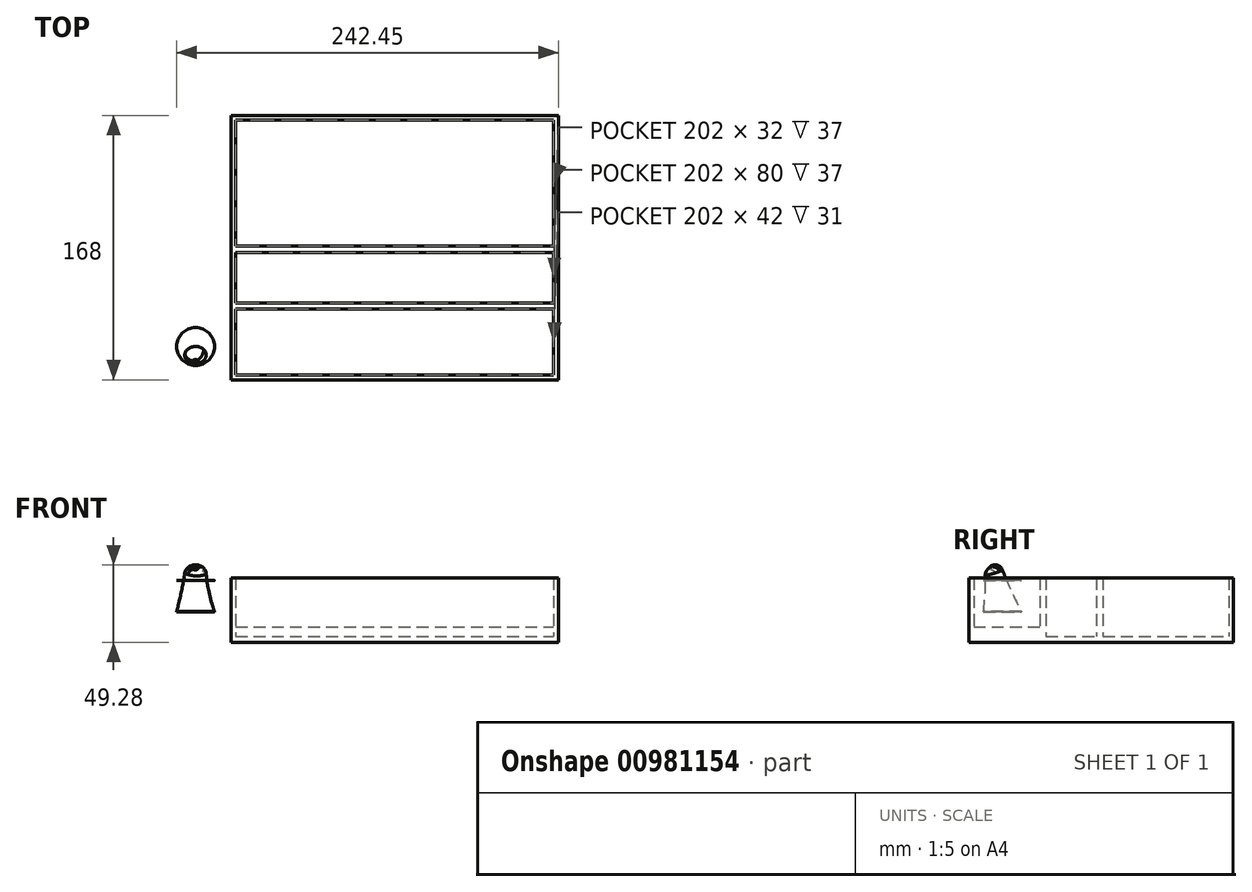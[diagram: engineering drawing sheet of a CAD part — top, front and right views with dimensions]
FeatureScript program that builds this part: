
annotation { "Feature Type Name" : "Feature", "Feature Type Description" : "" }
export const myFeature = defineFeature(function(context is Context, id is Id, definition is map)
    precondition{}
    {
        {
            var Q0;
            Q0=qCreatedBy(makeId("Top.planeOp"),FACE);
            var sketch = newSketch(context, id + "F0", { "sketchPlane" : qUnion([Q0])});
            skLineSegment(sketch, "E0.bottom", {"start": v(104, -84) * mm, "end": v(-104, -84) * mm});
            skLineSegment(sketch, "E0.top", {"start": v(104, 84) * mm, "end": v(-104, 84) * mm});
            skLineSegment(sketch, "E0.left", {"start": v(104, -84) * mm, "end": v(104, 84) * mm});
            skLineSegment(sketch, "E0.right", {"start": v(-104, -84) * mm, "end": v(-104, 84) * mm});
            skPoint(sketch, "E0.middle", {"position": v(0, 0) * mm});
            skSolve(sketch);
        }
        {
            var Q0;
            Q0=makeQuery(id+"F0.imprint","IMPRINT",FACE,{"disambiguationData":[TD([[makeQuery(id+"F0.imprint","IMPRINT",EDGE,{"derivedFrom":sQuery(id+"F0.wireOp",EDGE,"E0.bottom")}),-1.0]])]});
            extrude(context, id + "F1", {"entities" : qUnion([Q0]), "depth" : 4 * mm, "offsetDistance" : 25 * mm});
        }
        {
            var Q0;
            Q0=makeQuery(id+"F1.opExtrude","CAP_FACE",FACE,{"disambiguationData":[OSD([sQuery(id+"F0.wireOp",EDGE,"E0.bottom"),sQuery(id+"F0.wireOp",EDGE,"E0.top"),sQuery(id+"F0.wireOp",EDGE,"E0.left"),sQuery(id+"F0.wireOp",EDGE,"E0.right")])],"isStart":false});
            var sketch = newSketch(context, id + "F2", { "sketchPlane" : qUnion([Q0])});
            skLineSegment(sketch, "E1.bottom", {"start": v(104, -84) * mm, "end": v(-104, -84) * mm});
            skLineSegment(sketch, "E1.top", {"start": v(104, 84) * mm, "end": v(-104, 84) * mm});
            skLineSegment(sketch, "E1.left", {"start": v(104, -84) * mm, "end": v(104, 84) * mm});
            skLineSegment(sketch, "E1.right", {"start": v(-104, -84) * mm, "end": v(-104, 84) * mm});
            skPoint(sketch, "E1.middle", {"position": v(0, 0) * mm});
            skLineSegment(sketch, "E2.bottom", {"start": v(101, -81) * mm, "end": v(-101, -81) * mm});
            skLineSegment(sketch, "E2.top", {"start": v(101, 81) * mm, "end": v(-101, 81) * mm});
            skLineSegment(sketch, "E2.left", {"start": v(101, -81) * mm, "end": v(101, 81) * mm});
            skLineSegment(sketch, "E2.right", {"start": v(-101, -81) * mm, "end": v(-101, 81) * mm});
            skLineSegment(sketch, "E3", {"start": v(-101, 81) * mm, "end": v(-101, 41) * mm, "construction": true});
            skLineSegment(sketch, "E4", {"start": v(-101, 41) * mm, "end": v(-101, 1) * mm, "construction": true});
            skLineSegment(sketch, "E5", {"start": v(-101, 1) * mm, "end": v(-101, -35) * mm, "construction": true});
            skLineSegment(sketch, "E6.bottom", {"start": v(-101, 41) * mm, "end": v(101, 41) * mm});
            skLineSegment(sketch, "E6.top", {"start": v(-101, 37) * mm, "end": v(101, 37) * mm});
            skLineSegment(sketch, "E6.left", {"start": v(-101, 41) * mm, "end": v(-101, 37) * mm});
            skLineSegment(sketch, "E6.right", {"start": v(101, 41) * mm, "end": v(101, 37) * mm});
            skLineSegment(sketch, "E7.bottom", {"start": v(-101, 1) * mm, "end": v(101, 1) * mm});
            skLineSegment(sketch, "E7.top", {"start": v(-101, -3) * mm, "end": v(101, -3) * mm});
            skLineSegment(sketch, "E7.left", {"start": v(-101, 1) * mm, "end": v(-101, -3) * mm});
            skLineSegment(sketch, "E7.right", {"start": v(101, 1) * mm, "end": v(101, -3) * mm});
            skLineSegment(sketch, "E8.bottom", {"start": v(-101, -35) * mm, "end": v(101, -35) * mm});
            skLineSegment(sketch, "E8.top", {"start": v(-101, -39) * mm, "end": v(101, -39) * mm});
            skLineSegment(sketch, "E8.left", {"start": v(-101, -35) * mm, "end": v(-101, -39) * mm});
            skLineSegment(sketch, "E8.right", {"start": v(101, -35) * mm, "end": v(101, -39) * mm});
            skLineSegment(sketch, "E9", {"start": v(-101, 81) * mm, "end": v(-42, 81) * mm, "construction": true});
            skLineSegment(sketch, "E10", {"start": v(-42, 81) * mm, "end": v(-2, 81) * mm, "construction": true});
            skLineSegment(sketch, "E11", {"start": v(-2, 81) * mm, "end": v(38, 81) * mm, "construction": true});
            skLineSegment(sketch, "E12", {"start": v(38, 81) * mm, "end": v(101, 81) * mm, "construction": true});
            skLineSegment(sketch, "E13.bottom", {"start": v(-42, 81) * mm, "end": v(-38, 81) * mm});
            skLineSegment(sketch, "E13.top", {"start": v(-42, 41) * mm, "end": v(-38, 41) * mm});
            skLineSegment(sketch, "E13.left", {"start": v(-42, 81) * mm, "end": v(-42, 41) * mm});
            skLineSegment(sketch, "E13.right", {"start": v(-38, 81) * mm, "end": v(-38, 41) * mm});
            skLineSegment(sketch, "E14.bottom", {"start": v(-2, 81) * mm, "end": v(2, 81) * mm});
            skLineSegment(sketch, "E14.top", {"start": v(-2, 41) * mm, "end": v(2, 41) * mm});
            skLineSegment(sketch, "E15.bottom", {"start": v(38, 81) * mm, "end": v(42, 81) * mm});
            skLineSegment(sketch, "E15.top", {"start": v(38, 41) * mm, "end": v(42, 41) * mm});
            skLineSegment(sketch, "E15.left", {"start": v(38, 81) * mm, "end": v(38, 41) * mm});
            skLineSegment(sketch, "E15.right", {"start": v(42, 81) * mm, "end": v(42, 41) * mm});
            skLineSegment(sketch, "E16.bottom", {"start": v(-2, 37) * mm, "end": v(2, 37) * mm});
            skLineSegment(sketch, "E16.top", {"start": v(-2, 1) * mm, "end": v(2, 1) * mm});
            skLineSegment(sketch, "E16.left", {"start": v(-2, 37) * mm, "end": v(-2, 1) * mm});
            skLineSegment(sketch, "E16.right", {"start": v(2, 37) * mm, "end": v(2, 1) * mm});
            skSolve(sketch);
        }
        {
            var Q0;
            Q0=makeQuery(id+"F2.imprint","IMPRINT",FACE,{"disambiguationData":[TD([[makeQuery(id+"F2.imprint","IMPRINT",EDGE,{"derivedFrom":sQuery(id+"F2.wireOp",EDGE,"E1.bottom")}),-1.0]])]});
            var Q1;
            {var subQ2=sQuery(id+"F2.wireOp",EDGE,"E6.left");Q1=makeQuery(id+"F2.imprint","IMPRINT",FACE,{"disambiguationData":[TD([[makeQuery(id+"F2.imprint","IMPRINT",EDGE,{"derivedFrom":subQ2}),1.0]])]});}
            var Q2;
            Q2=makeQuery(id+"F2.imprint","IMPRINT",FACE,{"disambiguationData":[TD([[makeQuery(id+"F2.imprint","IMPRINT",EDGE,{"derivedFrom":sQuery(id+"F2.wireOp",EDGE,"E13.bottom")}),-1.0]])]});
            var Q3;
            Q3=makeQuery(id+"F2.imprint","IMPRINT",FACE,{"disambiguationData":[TD([[makeQuery(id+"F2.imprint","IMPRINT",EDGE,{"derivedFrom":sQuery(id+"F2.wireOp",EDGE,"E15.bottom")}),-1.0]])]});
            var Q4;
            Q4=makeQuery(id+"F2.imprint","IMPRINT",FACE,{"disambiguationData":[TD([[makeQuery(id+"F2.imprint","IMPRINT",EDGE,{"derivedFrom":sQuery(id+"F2.wireOp",EDGE,"E16.bottom")}),-1.0]])]});
            var Q5;
            Q5=makeQuery(id+"F2.imprint","IMPRINT",FACE,{"disambiguationData":[TD([[makeQuery(id+"F2.imprint","IMPRINT",EDGE,{"derivedFrom":sQuery(id+"F2.wireOp",EDGE,"E7.top")}),1.0]])]});
            var Q6;
            Q6=makeQuery(id+"F2.imprint","IMPRINT",FACE,{"disambiguationData":[TD([[makeQuery(id+"F2.imprint","IMPRINT",EDGE,{"derivedFrom":sQuery(id+"F2.wireOp",EDGE,"E8.bottom")}),-1.0]])]});
            extrude(context, id + "F3", {"entities" : qUnion([Q0, Q1, Q2, Q3, Q4, Q5, Q6]), "operationType" : NewBodyOperationType.ADD, "depth" : 37 * mm, "offsetDistance" : 25 * mm});
        }
        {
            var Q0;
            {var subQ0=sQuery(id+"F2.wireOp",EDGE,"E2.bottom");Q0=makeQuery(id+"F3.boolean.opBoolean","SPLIT",FACE,{"disambiguationData":[TD([makeQuery(id+"F3.opExtrude","SWEPT_FACE",FACE,{"disambiguationData":[OSD([subQ0])]})])],"derivedFrom":makeQuery(id+"F1.opExtrude","CAP_FACE",FACE,{"disambiguationData":[OSD([sQuery(id+"F0.wireOp",EDGE,"E0.bottom"),sQuery(id+"F0.wireOp",EDGE,"E0.top"),sQuery(id+"F0.wireOp",EDGE,"E0.left"),sQuery(id+"F0.wireOp",EDGE,"E0.right")])],"isStart":false})});}
            extrude(context, id + "F4", {"entities" : qUnion([Q0]), "operationType" : NewBodyOperationType.ADD, "depth" : 6 * mm, "offsetDistance" : 25 * mm});
        }
        {
            var Q0;
            Q0=makeQuery(id+"F4.opExtrude","CAP_FACE",FACE,{"disambiguationData":[OSD([sQuery(id+"F0.wireOp",EDGE,"E0.bottom"),sQuery(id+"F0.wireOp",EDGE,"E0.top"),sQuery(id+"F0.wireOp",EDGE,"E0.left"),sQuery(id+"F0.wireOp",EDGE,"E0.right")])],"isStart":false});
            cPlane(context, id + "F5", {"entities" : qUnion([Q0]), "cplaneType" : CPlaneType.OFFSET, "offset" : 9.5 * mm, "width" : 150 * mm, "height" : 150 * mm});
        }
        {
            var Q0;
            Q0=qCreatedBy(id+"F5.planeOp",FACE);
            var sketch = newSketch(context, id + "F6", { "sketchPlane" : qUnion([Q0])});
            skCircle(sketch, "E17", {"center": v(-126.45, -62.76) * mm, "radius": 12 * mm});
            skSolve(sketch);
        }
        {
            var Q0;
            Q0=makeQuery(id+"F6.imprint","IMPRINT",FACE,{"disambiguationData":[TD([[makeQuery(id+"F6.imprint","IMPRINT",EDGE,{"derivedFrom":sQuery(id+"F6.wireOp",EDGE,"E17")}),1.0]])]});
            extrude(context, id + "F7", {"entities" : qUnion([Q0]), "depth" : .1 * mm, "offsetDistance" : 25 * mm});
        }
        {
            var Q0;
            Q0=makeQuery(id+"F7.opExtrude","SWEPT_BODY",BODY,{"disambiguationData":[OSD([sQuery(id+"F6.wireOp",EDGE,"E17")])]});
            transform(context, id + "F8", {"entities" : qUnion([Q0]), "transformType" : TransformType.TRANSLATION_3D, "dx" : 0 * mm, "dy" : 0 * mm, "dz" : 3.9 * mm, "makeCopy" : true});
        }
        {
            var Q0;
            Q0=makeQuery(id+"F8.opPattern","COPY",BODY,{"derivedFrom":makeQuery(id+"F7.opExtrude","SWEPT_BODY",BODY,{"disambiguationData":[OSD([sQuery(id+"F6.wireOp",EDGE,"E17")])]}),"instanceName":"1"});
            transform(context, id + "F9", {"entities" : qUnion([Q0]), "transformType" : TransformType.TRANSLATION_3D, "dx" : 0 * mm, "dy" : 0 * mm, "dz" : 16 * mm, "makeCopy" : true});
        }
        {
            var Q0;
            Q0=makeQuery(id+"F9.opPattern","COPY",FACE,{"derivedFrom":makeQuery(id+"F8.opPattern","COPY",FACE,{"derivedFrom":makeQuery(id+"F7.opExtrude","CAP_FACE",FACE,{"disambiguationData":[OSD([sQuery(id+"F6.wireOp",EDGE,"E17")])],"isStart":false}),"instanceName":"1"}),"instanceName":"1"});
            var sketch = newSketch(context, id + "F10", { "sketchPlane" : qUnion([Q0])});
            skCircle(sketch, "E18", {"center": v(-126.45, -62.76) * mm, "radius": 6.5 * mm});
            skSolve(sketch);
        }
        {
            var Q0;
            Q0=makeQuery(id+"F10.imprint","IMPRINT",FACE,{"disambiguationData":[TD([[makeQuery(id+"F10.imprint","IMPRINT",EDGE,{"derivedFrom":sQuery(id+"F10.wireOp",EDGE,"E18")}),1.0]])]});
            extrude(context, id + "F11", {"entities" : qUnion([Q0]), "depth" : .1 * mm, "offsetDistance" : 25 * mm});
        }
        {
            var Q0;
            Q0=makeQuery(id+"F11.opExtrude","SWEPT_BODY",BODY,{"disambiguationData":[OSD([sQuery(id+"F10.wireOp",EDGE,"E18")])]});
            transform(context, id + "F12", {"entities" : qUnion([Q0]), "transformType" : TransformType.TRANSLATION_3D, "dx" : 0 * mm, "dy" : 0 * mm, "dz" : 7.2 * mm, "makeCopy" : false});
        }
        {
            var Q0;
            Q0=makeQuery(id+"F3.opExtrude","SWEPT_FACE",FACE,{"disambiguationData":[OSD([sQuery(id+"F2.wireOp",EDGE,"E8.top")])]});
            cPlane(context, id + "F13", {"entities" : qUnion([Q0]), "cplaneType" : CPlaneType.OFFSET, "offset" : 24.4 * mm, "width" : 150 * mm, "height" : 150 * mm});
        }
        {
            var Q0;
            Q0=makeQuery(id+"F11.opExtrude","CAP_FACE",FACE,{"disambiguationData":[OSD([sQuery(id+"F10.wireOp",EDGE,"E18")])],"isStart":false});
            var sketch = newSketch(context, id + "F14", { "sketchPlane" : qUnion([Q0])});
            skLineSegment(sketch, "E19", {"start": v(-138.54, -62.76) * mm, "end": v(-113.11, -62.76) * mm, "construction": true});
            skSolve(sketch);
        }
        {
            var Q0;
            Q0=makeQuery(id+"F11.opExtrude","SWEPT_BODY",BODY,{"disambiguationData":[OSD([sQuery(id+"F10.wireOp",EDGE,"E18")])]});
            var Q1;
            Q1=sQuery(id+"F14.wireOp",EDGE,"E19");
            transform(context, id + "F15", {"entities" : qUnion([Q0]), "transformType" : TransformType.ROTATION, "transformAxis" : qUnion([Q1]), "angle" : 48 * degree, "makeCopy" : false});
        }
        {
            var Q0;
            Q0=makeQuery(id+"F11.opExtrude","SWEPT_BODY",BODY,{"disambiguationData":[OSD([sQuery(id+"F10.wireOp",EDGE,"E18")])]});
            transform(context, id + "F16", {"entities" : qUnion([Q0]), "transformType" : TransformType.TRANSLATION_3D, "dx" : 0 * mm, "dy" : -7 * mm, "dz" : 2.5 * mm, "makeCopy" : false});
        }
        {
            var Q0;
            Q0=makeQuery(id+"F7.opExtrude","CAP_FACE",FACE,{"disambiguationData":[OSD([sQuery(id+"F6.wireOp",EDGE,"E17")])],"isStart":false});
            var Q1;
            Q1=makeQuery(id+"F11.opExtrude","CAP_FACE",FACE,{"disambiguationData":[OSD([sQuery(id+"F10.wireOp",EDGE,"E18")])],"isStart":true});
            loft(context, id + "F17", {"sheetProfilesArray" : [{ "sheetProfileEntities" : qUnion([Q0]) }, { "sheetProfileEntities" : qUnion([Q1]) }]});
        }
        {
            var Q0;
            Q0=makeQuery(id+"F11.opExtrude","SWEPT_BODY",BODY,{"disambiguationData":[OSD([sQuery(id+"F10.wireOp",EDGE,"E18")])]});
            deleteBodies(context, id + "F18", {"entities" : qUnion([Q0])});
        }
        {
            var Q0;
            Q0=makeQuery(id+"F8.opPattern","COPY",BODY,{"derivedFrom":makeQuery(id+"F7.opExtrude","SWEPT_BODY",BODY,{"disambiguationData":[OSD([sQuery(id+"F6.wireOp",EDGE,"E17")])]}),"instanceName":"1"});
            deleteBodies(context, id + "F19", {"entities" : qUnion([Q0])});
        }
        {
            var Q0;
            Q0=makeQuery(id+"F17.opLoft","MID_CAP_EDGE",EDGE,{"disambiguationData":[OSD([sQuery(id+"F10.wireOp",EDGE,"E18")])],"capPos":1.0});
            fillet(context, id + "F20", {"entities" : qUnion([Q0]), "tangentPropagation" : true, "radius" : 5 * mm, "defaultsChanged" : false, "vertexSettings" : [], "allowEdgeOverflow" : false});
        }
    });
